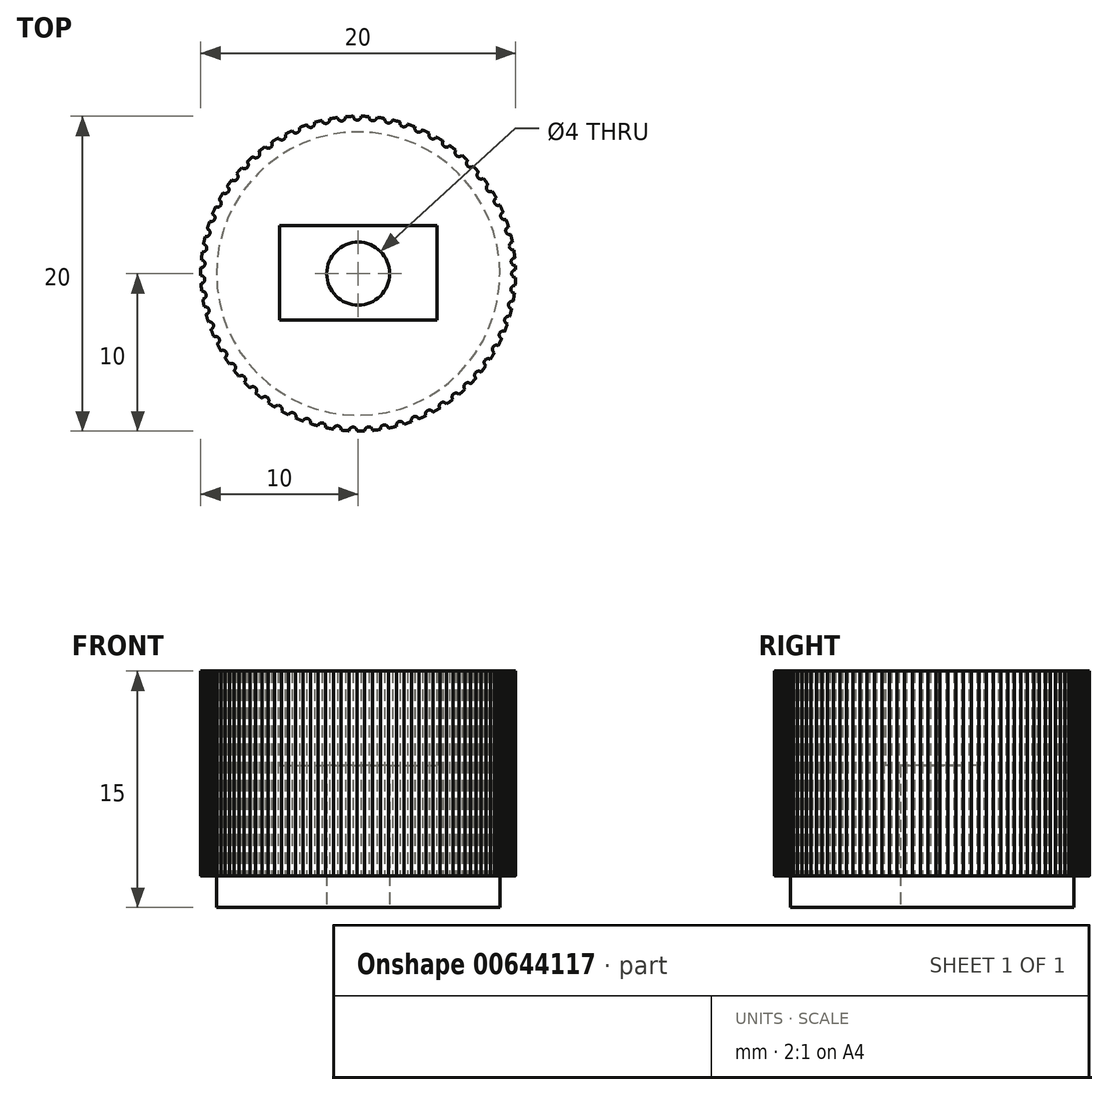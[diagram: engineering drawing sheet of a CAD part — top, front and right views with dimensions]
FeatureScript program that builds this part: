
annotation { "Feature Type Name" : "Feature", "Feature Type Description" : "" }
export const myFeature = defineFeature(function(context is Context, id is Id, definition is map)
    precondition{}
    {
        {
            var Q0;
            Q0=qCreatedBy(makeId("Top.planeOp"),FACE);
            var sketch = newSketch(context, id + "F0", { "sketchPlane" : qUnion([Q0])});
            skCircle(sketch, "E0", {"center": v(0, 0) * mm, "radius": 10 * mm});
            skLineSegment(sketch, "E1.bottom", {"start": v(-5, 3.04) * mm, "end": v(5, 3.04) * mm});
            skLineSegment(sketch, "E1.top", {"start": v(-5, -2.96) * mm, "end": v(5, -2.96) * mm});
            skLineSegment(sketch, "E1.left", {"start": v(-5, 3.04) * mm, "end": v(-5, -2.96) * mm});
            skLineSegment(sketch, "E1.right", {"start": v(5, 3.04) * mm, "end": v(5, -2.96) * mm});
            skCircle(sketch, "E2", {"center": v(0, 0) * mm, "radius": 2 * mm});
            skCircle(sketch, "E3", {"center": v(0, 0) * mm, "radius": 9 * mm});
            skCircle(sketch, "E4", {"center": v(10, 0) * mm, "radius": 0.25 * mm});
            skCircle(sketch, "E5", {"center": v(9.95, -1) * mm, "radius": 0.25 * mm});
            skCircle(sketch, "E6", {"center": v(9.8, -1.99) * mm, "radius": 0.25 * mm});
            skCircle(sketch, "E7", {"center": v(9.55, -2.96) * mm, "radius": 0.25 * mm});
            skCircle(sketch, "E8", {"center": v(9.2, -3.9) * mm, "radius": 0.25 * mm});
            skCircle(sketch, "E9", {"center": v(8.77, -4.8) * mm, "radius": 0.25 * mm});
            skCircle(sketch, "E10", {"center": v(8.25, -5.65) * mm, "radius": 0.25 * mm});
            skCircle(sketch, "E11", {"center": v(7.65, -6.45) * mm, "radius": 0.25 * mm});
            skCircle(sketch, "E12", {"center": v(6.96, -7.18) * mm, "radius": 0.25 * mm});
            skCircle(sketch, "E13", {"center": v(6.21, -7.84) * mm, "radius": 0.25 * mm});
            skCircle(sketch, "E14", {"center": v(5.4, -8.42) * mm, "radius": 0.25 * mm});
            skCircle(sketch, "E15", {"center": v(4.53, -8.91) * mm, "radius": 0.25 * mm});
            skCircle(sketch, "E16", {"center": v(3.62, -9.32) * mm, "radius": 0.25 * mm});
            skCircle(sketch, "E17", {"center": v(2.67, -9.64) * mm, "radius": 0.25 * mm});
            skCircle(sketch, "E18", {"center": v(1.67, -9.86) * mm, "radius": 0.25 * mm});
            skCircle(sketch, "E19", {"center": v(0.67, -9.98) * mm, "radius": 0.25 * mm});
            skCircle(sketch, "E20", {"center": v(-1.33, -9.91) * mm, "radius": 0.25 * mm});
            skCircle(sketch, "E21", {"center": v(-2.31, -9.73) * mm, "radius": 0.25 * mm});
            skCircle(sketch, "E22", {"center": v(-3.27, -9.45) * mm, "radius": 0.25 * mm});
            skCircle(sketch, "E23", {"center": v(-4.2, -9.08) * mm, "radius": 0.25 * mm});
            skCircle(sketch, "E24", {"center": v(-5.08, -8.61) * mm, "radius": 0.25 * mm});
            skCircle(sketch, "E25", {"center": v(-5.92, -8.06) * mm, "radius": 0.25 * mm});
            skCircle(sketch, "E26", {"center": v(-6.7, -7.43) * mm, "radius": 0.25 * mm});
            skCircle(sketch, "E27", {"center": v(-7.4, -6.72) * mm, "radius": 0.25 * mm});
            skCircle(sketch, "E28", {"center": v(-8.04, -5.95) * mm, "radius": 0.25 * mm});
            skCircle(sketch, "E29", {"center": v(-8.6, -5.12) * mm, "radius": 0.25 * mm});
            skCircle(sketch, "E30", {"center": v(-9.06, -4.23) * mm, "radius": 0.25 * mm});
            skCircle(sketch, "E31", {"center": v(-0.33, -10) * mm, "radius": 0.25 * mm});
            skCircle(sketch, "E32", {"center": v(-9.44, -3.3) * mm, "radius": 0.25 * mm});
            skCircle(sketch, "E33", {"center": v(-9.72, -2.35) * mm, "radius": 0.25 * mm});
            skCircle(sketch, "E34", {"center": v(-9.9, -1.37) * mm, "radius": 0.25 * mm});
            skCircle(sketch, "E35", {"center": v(-9.98, 0.63) * mm, "radius": 0.25 * mm});
            skCircle(sketch, "E36", {"center": v(-9.87, 1.62) * mm, "radius": 0.25 * mm});
            skCircle(sketch, "E37", {"center": v(-9.66, 2.6) * mm, "radius": 0.25 * mm});
            skCircle(sketch, "E38", {"center": v(-9.35, 3.55) * mm, "radius": 0.25 * mm});
            skCircle(sketch, "E39", {"center": v(-8.95, 4.47) * mm, "radius": 0.25 * mm});
            skCircle(sketch, "E40", {"center": v(-8.46, 5.34) * mm, "radius": 0.25 * mm});
            skCircle(sketch, "E41", {"center": v(-7.88, 6.16) * mm, "radius": 0.25 * mm});
            skCircle(sketch, "E42", {"center": v(-7.23, 6.91) * mm, "radius": 0.25 * mm});
            skCircle(sketch, "E43", {"center": v(-5.7, 8.21) * mm, "radius": 0.25 * mm});
            skCircle(sketch, "E44", {"center": v(-4.86, 8.74) * mm, "radius": 0.25 * mm});
            skCircle(sketch, "E45", {"center": v(-3.96, 9.18) * mm, "radius": 0.25 * mm});
            skCircle(sketch, "E46", {"center": v(-10, -0.37) * mm, "radius": 0.25 * mm});
            skCircle(sketch, "E47", {"center": v(-6.5, 7.6) * mm, "radius": 0.25 * mm});
            skCircle(sketch, "E48", {"center": v(-3.02, 9.53) * mm, "radius": 0.25 * mm});
            skCircle(sketch, "E49", {"center": v(-2.06, 9.79) * mm, "radius": 0.25 * mm});
            skCircle(sketch, "E50", {"center": v(-1.06, 9.94) * mm, "radius": 0.25 * mm});
            skCircle(sketch, "E51", {"center": v(-0.06, 10) * mm, "radius": 0.25 * mm});
            skCircle(sketch, "E52", {"center": v(0.94, 9.96) * mm, "radius": 0.25 * mm});
            skCircle(sketch, "E53", {"center": v(1.93, 9.81) * mm, "radius": 0.25 * mm});
            skCircle(sketch, "E54", {"center": v(2.9, 9.57) * mm, "radius": 0.25 * mm});
            skCircle(sketch, "E55", {"center": v(3.84, 9.23) * mm, "radius": 0.25 * mm});
            skCircle(sketch, "E56", {"center": v(4.75, 8.8) * mm, "radius": 0.25 * mm});
            skCircle(sketch, "E57", {"center": v(5.6, 8.28) * mm, "radius": 0.25 * mm});
            skCircle(sketch, "E58", {"center": v(6.4, 7.68) * mm, "radius": 0.25 * mm});
            skCircle(sketch, "E59", {"center": v(7.14, 7) * mm, "radius": 0.25 * mm});
            skCircle(sketch, "E60", {"center": v(7.8, 6.26) * mm, "radius": 0.25 * mm});
            skCircle(sketch, "E61", {"center": v(8.39, 5.45) * mm, "radius": 0.25 * mm});
            skCircle(sketch, "E62", {"center": v(8.89, 4.58) * mm, "radius": 0.25 * mm});
            skCircle(sketch, "E63", {"center": v(9.3, 3.67) * mm, "radius": 0.25 * mm});
            skCircle(sketch, "E64", {"center": v(9.62, 2.73) * mm, "radius": 0.25 * mm});
            skCircle(sketch, "E65", {"center": v(9.85, 1.75) * mm, "radius": 0.25 * mm});
            skCircle(sketch, "E66", {"center": v(9.97, 0.76) * mm, "radius": 0.25 * mm});
            skSolve(sketch);
        }
        {
            var Q0;
            Q0=makeQuery(id+"F0.imprint","IMPRINT",FACE,{"disambiguationData":[TD([[makeQuery(id+"F0.imprint","IMPRINT",EDGE,{"derivedFrom":sQuery(id+"F0.wireOp",EDGE,"E1.bottom")}),-1.0]])]});
            var Q1;
            Q1=makeQuery(id+"F0.imprint","IMPRINT",FACE,{"disambiguationData":[TD([[makeQuery(id+"F0.imprint","IMPRINT",EDGE,{"derivedFrom":sQuery(id+"F0.wireOp",EDGE,"E1.bottom")}),1.0]])]});
            extrude(context, id + "F1", {"entities" : qUnion([Q0, Q1]), "depth" : 15 * mm, "offsetDistance" : 25 * mm});
        }
        {
            var Q0;
            Q0=makeQuery(id+"F0.imprint","IMPRINT",FACE,{"disambiguationData":[TD([[makeQuery(id+"F0.imprint","IMPRINT",EDGE,{"derivedFrom":sQuery(id+"F0.wireOp",EDGE,"E0")}),1.0]])]});
            extrude(context, id + "F2", {"entities" : qUnion([Q0]), "operationType" : NewBodyOperationType.ADD, "depth" : 15 * mm, "offsetDistance" : 25 * mm, "hasSecondDirection" : true, "secondDirectionOppositeDirection" : false, "secondDirectionDepth" : 2 * mm});
        }
        {
            var Q0;
            Q0=makeQuery(id+"F0.imprint","IMPRINT",FACE,{"disambiguationData":[TD([[makeQuery(id+"F0.imprint","IMPRINT",EDGE,{"derivedFrom":sQuery(id+"F0.wireOp",EDGE,"E1.bottom")}),-1.0]])]});
            extrude(context, id + "F3", {"entities" : qUnion([Q0]), "operationType" : NewBodyOperationType.REMOVE, "depth" : 15 * mm, "offsetDistance" : 25 * mm, "hasSecondDirection" : true, "secondDirectionOppositeDirection" : false, "secondDirectionDepth" : 9 * mm});
        }
        {
            var Q0;
            {var subQ0=sQuery(id+"F0.wireOp",EDGE,"E4");var subQ1=sQuery(id+"F0.wireOp",EDGE,"E0");var subQ2=makeQuery(id+"F0.imprint","INTERSECT",VERTEX,{"disambiguationData":[OD(0.0)],"derivedFrom":[subQ1,subQ0]});Q0=makeQuery(id+"F0.imprint","IMPRINT",FACE,{"disambiguationData":[TD([[makeQuery(id+"F0.imprint","IMPRINT",EDGE,{"disambiguationData":[TD([[subQ2,1.0]])],"derivedFrom":subQ1}),1.0]])]});}
            var Q1;
            {var subQ0=sQuery(id+"F0.wireOp",EDGE,"E5");var subQ1=sQuery(id+"F0.wireOp",EDGE,"E0");var subQ2=makeQuery(id+"F0.imprint","INTERSECT",VERTEX,{"disambiguationData":[OD(0.0)],"derivedFrom":[subQ1,subQ0]});Q1=makeQuery(id+"F0.imprint","IMPRINT",FACE,{"disambiguationData":[TD([[makeQuery(id+"F0.imprint","IMPRINT",EDGE,{"disambiguationData":[TD([[subQ2,-1.0]])],"derivedFrom":subQ1}),1.0]])]});}
            var Q2;
            {var subQ0=sQuery(id+"F0.wireOp",EDGE,"E6");var subQ1=sQuery(id+"F0.wireOp",EDGE,"E0");var subQ2=makeQuery(id+"F0.imprint","INTERSECT",VERTEX,{"disambiguationData":[OD(0.0)],"derivedFrom":[subQ1,subQ0]});Q2=makeQuery(id+"F0.imprint","IMPRINT",FACE,{"disambiguationData":[TD([[makeQuery(id+"F0.imprint","IMPRINT",EDGE,{"disambiguationData":[TD([[subQ2,-1.0]])],"derivedFrom":subQ1}),1.0]])]});}
            extrude(context, id + "F4", {"entities" : qUnion([Q0, Q1, Q2]), "operationType" : NewBodyOperationType.REMOVE, "oppositeDirection" : true, "depth" : 25 * mm, "offsetDistance" : 25 * mm});
        }
        {
            var Q0;
            {var subQ0=sQuery(id+"F0.wireOp",EDGE,"E43");var subQ1=sQuery(id+"F0.wireOp",EDGE,"E0");var subQ2=makeQuery(id+"F0.imprint","INTERSECT",VERTEX,{"disambiguationData":[OD(0.0)],"derivedFrom":[subQ1,subQ0]});Q0=makeQuery(id+"F0.imprint","IMPRINT",FACE,{"disambiguationData":[TD([[makeQuery(id+"F0.imprint","IMPRINT",EDGE,{"disambiguationData":[TD([[subQ2,-1.0]])],"derivedFrom":subQ1}),1.0]])]});}
            var Q1;
            {var subQ0=sQuery(id+"F0.wireOp",EDGE,"E47");var subQ1=sQuery(id+"F0.wireOp",EDGE,"E0");var subQ2=makeQuery(id+"F0.imprint","INTERSECT",VERTEX,{"disambiguationData":[OD(0.0)],"derivedFrom":[subQ1,subQ0]});Q1=makeQuery(id+"F0.imprint","IMPRINT",FACE,{"disambiguationData":[TD([[makeQuery(id+"F0.imprint","IMPRINT",EDGE,{"disambiguationData":[TD([[subQ2,-1.0]])],"derivedFrom":subQ1}),1.0]])]});}
            var Q2;
            {var subQ0=sQuery(id+"F0.wireOp",EDGE,"E42");var subQ1=sQuery(id+"F0.wireOp",EDGE,"E0");var subQ2=makeQuery(id+"F0.imprint","INTERSECT",VERTEX,{"disambiguationData":[OD(0.0)],"derivedFrom":[subQ1,subQ0]});Q2=makeQuery(id+"F0.imprint","IMPRINT",FACE,{"disambiguationData":[TD([[makeQuery(id+"F0.imprint","IMPRINT",EDGE,{"disambiguationData":[TD([[subQ2,-1.0]])],"derivedFrom":subQ1}),1.0]])]});}
            var Q3;
            {var subQ0=sQuery(id+"F0.wireOp",EDGE,"E41");var subQ1=sQuery(id+"F0.wireOp",EDGE,"E0");var subQ2=makeQuery(id+"F0.imprint","INTERSECT",VERTEX,{"disambiguationData":[OD(0.0)],"derivedFrom":[subQ1,subQ0]});Q3=makeQuery(id+"F0.imprint","IMPRINT",FACE,{"disambiguationData":[TD([[makeQuery(id+"F0.imprint","IMPRINT",EDGE,{"disambiguationData":[TD([[subQ2,-1.0]])],"derivedFrom":subQ1}),1.0]])]});}
            var Q4;
            {var subQ0=sQuery(id+"F0.wireOp",EDGE,"E40");var subQ1=sQuery(id+"F0.wireOp",EDGE,"E0");var subQ2=makeQuery(id+"F0.imprint","INTERSECT",VERTEX,{"disambiguationData":[OD(0.0)],"derivedFrom":[subQ1,subQ0]});Q4=makeQuery(id+"F0.imprint","IMPRINT",FACE,{"disambiguationData":[TD([[makeQuery(id+"F0.imprint","IMPRINT",EDGE,{"disambiguationData":[TD([[subQ2,-1.0]])],"derivedFrom":subQ1}),1.0]])]});}
            var Q5;
            {var subQ0=sQuery(id+"F0.wireOp",EDGE,"E39");var subQ1=sQuery(id+"F0.wireOp",EDGE,"E0");var subQ2=makeQuery(id+"F0.imprint","INTERSECT",VERTEX,{"disambiguationData":[OD(0.0)],"derivedFrom":[subQ1,subQ0]});Q5=makeQuery(id+"F0.imprint","IMPRINT",FACE,{"disambiguationData":[TD([[makeQuery(id+"F0.imprint","IMPRINT",EDGE,{"disambiguationData":[TD([[subQ2,-1.0]])],"derivedFrom":subQ1}),1.0]])]});}
            var Q6;
            {var subQ0=sQuery(id+"F0.wireOp",EDGE,"E38");var subQ1=sQuery(id+"F0.wireOp",EDGE,"E0");var subQ2=makeQuery(id+"F0.imprint","INTERSECT",VERTEX,{"disambiguationData":[OD(0.0)],"derivedFrom":[subQ1,subQ0]});Q6=makeQuery(id+"F0.imprint","IMPRINT",FACE,{"disambiguationData":[TD([[makeQuery(id+"F0.imprint","IMPRINT",EDGE,{"disambiguationData":[TD([[subQ2,-1.0]])],"derivedFrom":subQ1}),1.0]])]});}
            var Q7;
            {var subQ0=sQuery(id+"F0.wireOp",EDGE,"E37");var subQ1=sQuery(id+"F0.wireOp",EDGE,"E0");var subQ2=makeQuery(id+"F0.imprint","INTERSECT",VERTEX,{"disambiguationData":[OD(0.0)],"derivedFrom":[subQ1,subQ0]});Q7=makeQuery(id+"F0.imprint","IMPRINT",FACE,{"disambiguationData":[TD([[makeQuery(id+"F0.imprint","IMPRINT",EDGE,{"disambiguationData":[TD([[subQ2,-1.0]])],"derivedFrom":subQ1}),1.0]])]});}
            var Q8;
            {var subQ0=sQuery(id+"F0.wireOp",EDGE,"E36");var subQ1=sQuery(id+"F0.wireOp",EDGE,"E0");var subQ2=makeQuery(id+"F0.imprint","INTERSECT",VERTEX,{"disambiguationData":[OD(0.0)],"derivedFrom":[subQ1,subQ0]});Q8=makeQuery(id+"F0.imprint","IMPRINT",FACE,{"disambiguationData":[TD([[makeQuery(id+"F0.imprint","IMPRINT",EDGE,{"disambiguationData":[TD([[subQ2,-1.0]])],"derivedFrom":subQ1}),1.0]])]});}
            var Q9;
            {var subQ0=sQuery(id+"F0.wireOp",EDGE,"E35");var subQ1=sQuery(id+"F0.wireOp",EDGE,"E0");var subQ2=makeQuery(id+"F0.imprint","INTERSECT",VERTEX,{"disambiguationData":[OD(0.0)],"derivedFrom":[subQ1,subQ0]});Q9=makeQuery(id+"F0.imprint","IMPRINT",FACE,{"disambiguationData":[TD([[makeQuery(id+"F0.imprint","IMPRINT",EDGE,{"disambiguationData":[TD([[subQ2,-1.0]])],"derivedFrom":subQ1}),1.0]])]});}
            var Q10;
            {var subQ0=sQuery(id+"F0.wireOp",EDGE,"E46");var subQ1=sQuery(id+"F0.wireOp",EDGE,"E0");var subQ2=makeQuery(id+"F0.imprint","INTERSECT",VERTEX,{"disambiguationData":[OD(0.0)],"derivedFrom":[subQ1,subQ0]});Q10=makeQuery(id+"F0.imprint","IMPRINT",FACE,{"disambiguationData":[TD([[makeQuery(id+"F0.imprint","IMPRINT",EDGE,{"disambiguationData":[TD([[subQ2,-1.0]])],"derivedFrom":subQ1}),1.0]])]});}
            var Q11;
            {var subQ0=sQuery(id+"F0.wireOp",EDGE,"E34");var subQ1=sQuery(id+"F0.wireOp",EDGE,"E0");var subQ2=makeQuery(id+"F0.imprint","INTERSECT",VERTEX,{"disambiguationData":[OD(0.0)],"derivedFrom":[subQ1,subQ0]});Q11=makeQuery(id+"F0.imprint","IMPRINT",FACE,{"disambiguationData":[TD([[makeQuery(id+"F0.imprint","IMPRINT",EDGE,{"disambiguationData":[TD([[subQ2,-1.0]])],"derivedFrom":subQ1}),1.0]])]});}
            var Q12;
            {var subQ0=sQuery(id+"F0.wireOp",EDGE,"E33");var subQ1=sQuery(id+"F0.wireOp",EDGE,"E0");var subQ2=makeQuery(id+"F0.imprint","INTERSECT",VERTEX,{"disambiguationData":[OD(0.0)],"derivedFrom":[subQ1,subQ0]});Q12=makeQuery(id+"F0.imprint","IMPRINT",FACE,{"disambiguationData":[TD([[makeQuery(id+"F0.imprint","IMPRINT",EDGE,{"disambiguationData":[TD([[subQ2,-1.0]])],"derivedFrom":subQ1}),1.0]])]});}
            var Q13;
            {var subQ0=sQuery(id+"F0.wireOp",EDGE,"E32");var subQ1=sQuery(id+"F0.wireOp",EDGE,"E0");var subQ2=makeQuery(id+"F0.imprint","INTERSECT",VERTEX,{"disambiguationData":[OD(0.0)],"derivedFrom":[subQ1,subQ0]});Q13=makeQuery(id+"F0.imprint","IMPRINT",FACE,{"disambiguationData":[TD([[makeQuery(id+"F0.imprint","IMPRINT",EDGE,{"disambiguationData":[TD([[subQ2,-1.0]])],"derivedFrom":subQ1}),1.0]])]});}
            var Q14;
            {var subQ0=sQuery(id+"F0.wireOp",EDGE,"E30");var subQ1=sQuery(id+"F0.wireOp",EDGE,"E0");var subQ2=makeQuery(id+"F0.imprint","INTERSECT",VERTEX,{"disambiguationData":[OD(0.0)],"derivedFrom":[subQ1,subQ0]});Q14=makeQuery(id+"F0.imprint","IMPRINT",FACE,{"disambiguationData":[TD([[makeQuery(id+"F0.imprint","IMPRINT",EDGE,{"disambiguationData":[TD([[subQ2,-1.0]])],"derivedFrom":subQ1}),1.0]])]});}
            var Q15;
            {var subQ0=sQuery(id+"F0.wireOp",EDGE,"E29");var subQ1=sQuery(id+"F0.wireOp",EDGE,"E0");var subQ2=makeQuery(id+"F0.imprint","INTERSECT",VERTEX,{"disambiguationData":[OD(0.0)],"derivedFrom":[subQ1,subQ0]});Q15=makeQuery(id+"F0.imprint","IMPRINT",FACE,{"disambiguationData":[TD([[makeQuery(id+"F0.imprint","IMPRINT",EDGE,{"disambiguationData":[TD([[subQ2,-1.0]])],"derivedFrom":subQ1}),1.0]])]});}
            var Q16;
            {var subQ0=sQuery(id+"F0.wireOp",EDGE,"E28");var subQ1=sQuery(id+"F0.wireOp",EDGE,"E0");var subQ2=makeQuery(id+"F0.imprint","INTERSECT",VERTEX,{"disambiguationData":[OD(0.0)],"derivedFrom":[subQ1,subQ0]});Q16=makeQuery(id+"F0.imprint","IMPRINT",FACE,{"disambiguationData":[TD([[makeQuery(id+"F0.imprint","IMPRINT",EDGE,{"disambiguationData":[TD([[subQ2,-1.0]])],"derivedFrom":subQ1}),1.0]])]});}
            var Q17;
            {var subQ0=sQuery(id+"F0.wireOp",EDGE,"E27");var subQ1=sQuery(id+"F0.wireOp",EDGE,"E0");var subQ2=makeQuery(id+"F0.imprint","INTERSECT",VERTEX,{"disambiguationData":[OD(0.0)],"derivedFrom":[subQ1,subQ0]});Q17=makeQuery(id+"F0.imprint","IMPRINT",FACE,{"disambiguationData":[TD([[makeQuery(id+"F0.imprint","IMPRINT",EDGE,{"disambiguationData":[TD([[subQ2,-1.0]])],"derivedFrom":subQ1}),1.0]])]});}
            var Q18;
            {var subQ0=sQuery(id+"F0.wireOp",EDGE,"E26");var subQ1=sQuery(id+"F0.wireOp",EDGE,"E0");var subQ2=makeQuery(id+"F0.imprint","INTERSECT",VERTEX,{"disambiguationData":[OD(0.0)],"derivedFrom":[subQ1,subQ0]});Q18=makeQuery(id+"F0.imprint","IMPRINT",FACE,{"disambiguationData":[TD([[makeQuery(id+"F0.imprint","IMPRINT",EDGE,{"disambiguationData":[TD([[subQ2,-1.0]])],"derivedFrom":subQ1}),1.0]])]});}
            var Q19;
            {var subQ0=sQuery(id+"F0.wireOp",EDGE,"E25");var subQ1=sQuery(id+"F0.wireOp",EDGE,"E0");var subQ2=makeQuery(id+"F0.imprint","INTERSECT",VERTEX,{"disambiguationData":[OD(0.0)],"derivedFrom":[subQ1,subQ0]});Q19=makeQuery(id+"F0.imprint","IMPRINT",FACE,{"disambiguationData":[TD([[makeQuery(id+"F0.imprint","IMPRINT",EDGE,{"disambiguationData":[TD([[subQ2,-1.0]])],"derivedFrom":subQ1}),1.0]])]});}
            var Q20;
            {var subQ0=sQuery(id+"F0.wireOp",EDGE,"E24");var subQ1=sQuery(id+"F0.wireOp",EDGE,"E0");var subQ2=makeQuery(id+"F0.imprint","INTERSECT",VERTEX,{"disambiguationData":[OD(0.0)],"derivedFrom":[subQ1,subQ0]});Q20=makeQuery(id+"F0.imprint","IMPRINT",FACE,{"disambiguationData":[TD([[makeQuery(id+"F0.imprint","IMPRINT",EDGE,{"disambiguationData":[TD([[subQ2,-1.0]])],"derivedFrom":subQ1}),1.0]])]});}
            var Q21;
            {var subQ0=sQuery(id+"F0.wireOp",EDGE,"E23");var subQ1=sQuery(id+"F0.wireOp",EDGE,"E0");var subQ2=makeQuery(id+"F0.imprint","INTERSECT",VERTEX,{"disambiguationData":[OD(0.0)],"derivedFrom":[subQ1,subQ0]});Q21=makeQuery(id+"F0.imprint","IMPRINT",FACE,{"disambiguationData":[TD([[makeQuery(id+"F0.imprint","IMPRINT",EDGE,{"disambiguationData":[TD([[subQ2,-1.0]])],"derivedFrom":subQ1}),1.0]])]});}
            var Q22;
            {var subQ0=sQuery(id+"F0.wireOp",EDGE,"E22");var subQ1=sQuery(id+"F0.wireOp",EDGE,"E0");var subQ2=makeQuery(id+"F0.imprint","INTERSECT",VERTEX,{"disambiguationData":[OD(0.0)],"derivedFrom":[subQ1,subQ0]});Q22=makeQuery(id+"F0.imprint","IMPRINT",FACE,{"disambiguationData":[TD([[makeQuery(id+"F0.imprint","IMPRINT",EDGE,{"disambiguationData":[TD([[subQ2,-1.0]])],"derivedFrom":subQ1}),1.0]])]});}
            var Q23;
            {var subQ0=sQuery(id+"F0.wireOp",EDGE,"E21");var subQ1=sQuery(id+"F0.wireOp",EDGE,"E0");var subQ2=makeQuery(id+"F0.imprint","INTERSECT",VERTEX,{"disambiguationData":[OD(0.0)],"derivedFrom":[subQ1,subQ0]});Q23=makeQuery(id+"F0.imprint","IMPRINT",FACE,{"disambiguationData":[TD([[makeQuery(id+"F0.imprint","IMPRINT",EDGE,{"disambiguationData":[TD([[subQ2,-1.0]])],"derivedFrom":subQ1}),1.0]])]});}
            var Q24;
            {var subQ0=sQuery(id+"F0.wireOp",EDGE,"E20");var subQ1=sQuery(id+"F0.wireOp",EDGE,"E0");var subQ2=makeQuery(id+"F0.imprint","INTERSECT",VERTEX,{"disambiguationData":[OD(0.0)],"derivedFrom":[subQ1,subQ0]});Q24=makeQuery(id+"F0.imprint","IMPRINT",FACE,{"disambiguationData":[TD([[makeQuery(id+"F0.imprint","IMPRINT",EDGE,{"disambiguationData":[TD([[subQ2,-1.0]])],"derivedFrom":subQ1}),1.0]])]});}
            var Q25;
            {var subQ0=sQuery(id+"F0.wireOp",EDGE,"E31");var subQ1=sQuery(id+"F0.wireOp",EDGE,"E0");var subQ2=makeQuery(id+"F0.imprint","INTERSECT",VERTEX,{"disambiguationData":[OD(0.0)],"derivedFrom":[subQ1,subQ0]});Q25=makeQuery(id+"F0.imprint","IMPRINT",FACE,{"disambiguationData":[TD([[makeQuery(id+"F0.imprint","IMPRINT",EDGE,{"disambiguationData":[TD([[subQ2,-1.0]])],"derivedFrom":subQ1}),1.0]])]});}
            var Q26;
            {var subQ0=sQuery(id+"F0.wireOp",EDGE,"E19");var subQ1=sQuery(id+"F0.wireOp",EDGE,"E0");var subQ2=makeQuery(id+"F0.imprint","INTERSECT",VERTEX,{"disambiguationData":[OD(0.0)],"derivedFrom":[subQ1,subQ0]});Q26=makeQuery(id+"F0.imprint","IMPRINT",FACE,{"disambiguationData":[TD([[makeQuery(id+"F0.imprint","IMPRINT",EDGE,{"disambiguationData":[TD([[subQ2,-1.0]])],"derivedFrom":subQ1}),1.0]])]});}
            var Q27;
            {var subQ0=sQuery(id+"F0.wireOp",EDGE,"E18");var subQ1=sQuery(id+"F0.wireOp",EDGE,"E0");var subQ2=makeQuery(id+"F0.imprint","INTERSECT",VERTEX,{"disambiguationData":[OD(0.0)],"derivedFrom":[subQ1,subQ0]});Q27=makeQuery(id+"F0.imprint","IMPRINT",FACE,{"disambiguationData":[TD([[makeQuery(id+"F0.imprint","IMPRINT",EDGE,{"disambiguationData":[TD([[subQ2,-1.0]])],"derivedFrom":subQ1}),1.0]])]});}
            var Q28;
            {var subQ0=sQuery(id+"F0.wireOp",EDGE,"E17");var subQ1=sQuery(id+"F0.wireOp",EDGE,"E0");var subQ2=makeQuery(id+"F0.imprint","INTERSECT",VERTEX,{"disambiguationData":[OD(0.0)],"derivedFrom":[subQ1,subQ0]});Q28=makeQuery(id+"F0.imprint","IMPRINT",FACE,{"disambiguationData":[TD([[makeQuery(id+"F0.imprint","IMPRINT",EDGE,{"disambiguationData":[TD([[subQ2,-1.0]])],"derivedFrom":subQ1}),1.0]])]});}
            var Q29;
            {var subQ0=sQuery(id+"F0.wireOp",EDGE,"E16");var subQ1=sQuery(id+"F0.wireOp",EDGE,"E0");var subQ2=makeQuery(id+"F0.imprint","INTERSECT",VERTEX,{"disambiguationData":[OD(0.0)],"derivedFrom":[subQ1,subQ0]});Q29=makeQuery(id+"F0.imprint","IMPRINT",FACE,{"disambiguationData":[TD([[makeQuery(id+"F0.imprint","IMPRINT",EDGE,{"disambiguationData":[TD([[subQ2,-1.0]])],"derivedFrom":subQ1}),1.0]])]});}
            var Q30;
            {var subQ0=sQuery(id+"F0.wireOp",EDGE,"E15");var subQ1=sQuery(id+"F0.wireOp",EDGE,"E0");var subQ2=makeQuery(id+"F0.imprint","INTERSECT",VERTEX,{"disambiguationData":[OD(0.0)],"derivedFrom":[subQ1,subQ0]});Q30=makeQuery(id+"F0.imprint","IMPRINT",FACE,{"disambiguationData":[TD([[makeQuery(id+"F0.imprint","IMPRINT",EDGE,{"disambiguationData":[TD([[subQ2,-1.0]])],"derivedFrom":subQ1}),1.0]])]});}
            var Q31;
            {var subQ0=sQuery(id+"F0.wireOp",EDGE,"E14");var subQ1=sQuery(id+"F0.wireOp",EDGE,"E0");var subQ2=makeQuery(id+"F0.imprint","INTERSECT",VERTEX,{"disambiguationData":[OD(0.0)],"derivedFrom":[subQ1,subQ0]});Q31=makeQuery(id+"F0.imprint","IMPRINT",FACE,{"disambiguationData":[TD([[makeQuery(id+"F0.imprint","IMPRINT",EDGE,{"disambiguationData":[TD([[subQ2,-1.0]])],"derivedFrom":subQ1}),1.0]])]});}
            var Q32;
            {var subQ0=sQuery(id+"F0.wireOp",EDGE,"E13");var subQ1=sQuery(id+"F0.wireOp",EDGE,"E0");var subQ2=makeQuery(id+"F0.imprint","INTERSECT",VERTEX,{"disambiguationData":[OD(0.0)],"derivedFrom":[subQ1,subQ0]});Q32=makeQuery(id+"F0.imprint","IMPRINT",FACE,{"disambiguationData":[TD([[makeQuery(id+"F0.imprint","IMPRINT",EDGE,{"disambiguationData":[TD([[subQ2,-1.0]])],"derivedFrom":subQ1}),1.0]])]});}
            var Q33;
            {var subQ0=sQuery(id+"F0.wireOp",EDGE,"E12");var subQ1=sQuery(id+"F0.wireOp",EDGE,"E0");var subQ2=makeQuery(id+"F0.imprint","INTERSECT",VERTEX,{"disambiguationData":[OD(0.0)],"derivedFrom":[subQ1,subQ0]});Q33=makeQuery(id+"F0.imprint","IMPRINT",FACE,{"disambiguationData":[TD([[makeQuery(id+"F0.imprint","IMPRINT",EDGE,{"disambiguationData":[TD([[subQ2,-1.0]])],"derivedFrom":subQ1}),1.0]])]});}
            var Q34;
            {var subQ0=sQuery(id+"F0.wireOp",EDGE,"E11");var subQ1=sQuery(id+"F0.wireOp",EDGE,"E0");var subQ2=makeQuery(id+"F0.imprint","INTERSECT",VERTEX,{"disambiguationData":[OD(0.0)],"derivedFrom":[subQ1,subQ0]});Q34=makeQuery(id+"F0.imprint","IMPRINT",FACE,{"disambiguationData":[TD([[makeQuery(id+"F0.imprint","IMPRINT",EDGE,{"disambiguationData":[TD([[subQ2,-1.0]])],"derivedFrom":subQ1}),1.0]])]});}
            var Q35;
            {var subQ0=sQuery(id+"F0.wireOp",EDGE,"E10");var subQ1=sQuery(id+"F0.wireOp",EDGE,"E0");var subQ2=makeQuery(id+"F0.imprint","INTERSECT",VERTEX,{"disambiguationData":[OD(0.0)],"derivedFrom":[subQ1,subQ0]});Q35=makeQuery(id+"F0.imprint","IMPRINT",FACE,{"disambiguationData":[TD([[makeQuery(id+"F0.imprint","IMPRINT",EDGE,{"disambiguationData":[TD([[subQ2,-1.0]])],"derivedFrom":subQ1}),1.0]])]});}
            var Q36;
            {var subQ0=sQuery(id+"F0.wireOp",EDGE,"E9");var subQ1=sQuery(id+"F0.wireOp",EDGE,"E0");var subQ2=makeQuery(id+"F0.imprint","INTERSECT",VERTEX,{"disambiguationData":[OD(0.0)],"derivedFrom":[subQ1,subQ0]});Q36=makeQuery(id+"F0.imprint","IMPRINT",FACE,{"disambiguationData":[TD([[makeQuery(id+"F0.imprint","IMPRINT",EDGE,{"disambiguationData":[TD([[subQ2,-1.0]])],"derivedFrom":subQ1}),1.0]])]});}
            var Q37;
            {var subQ0=sQuery(id+"F0.wireOp",EDGE,"E8");var subQ1=sQuery(id+"F0.wireOp",EDGE,"E0");var subQ2=makeQuery(id+"F0.imprint","INTERSECT",VERTEX,{"disambiguationData":[OD(0.0)],"derivedFrom":[subQ1,subQ0]});Q37=makeQuery(id+"F0.imprint","IMPRINT",FACE,{"disambiguationData":[TD([[makeQuery(id+"F0.imprint","IMPRINT",EDGE,{"disambiguationData":[TD([[subQ2,-1.0]])],"derivedFrom":subQ1}),1.0]])]});}
            var Q38;
            {var subQ0=sQuery(id+"F0.wireOp",EDGE,"E7");var subQ1=sQuery(id+"F0.wireOp",EDGE,"E0");var subQ2=makeQuery(id+"F0.imprint","INTERSECT",VERTEX,{"disambiguationData":[OD(0.0)],"derivedFrom":[subQ1,subQ0]});Q38=makeQuery(id+"F0.imprint","IMPRINT",FACE,{"disambiguationData":[TD([[makeQuery(id+"F0.imprint","IMPRINT",EDGE,{"disambiguationData":[TD([[subQ2,-1.0]])],"derivedFrom":subQ1}),1.0]])]});}
            var Q39;
            {var subQ0=sQuery(id+"F0.wireOp",EDGE,"E6");var subQ1=sQuery(id+"F0.wireOp",EDGE,"E0");var subQ2=makeQuery(id+"F0.imprint","INTERSECT",VERTEX,{"disambiguationData":[OD(0.0)],"derivedFrom":[subQ1,subQ0]});Q39=makeQuery(id+"F0.imprint","IMPRINT",FACE,{"disambiguationData":[TD([[makeQuery(id+"F0.imprint","IMPRINT",EDGE,{"disambiguationData":[TD([[subQ2,-1.0]])],"derivedFrom":subQ1}),1.0]])]});}
            var Q40;
            {var subQ0=sQuery(id+"F0.wireOp",EDGE,"E5");var subQ1=sQuery(id+"F0.wireOp",EDGE,"E0");var subQ2=makeQuery(id+"F0.imprint","INTERSECT",VERTEX,{"disambiguationData":[OD(0.0)],"derivedFrom":[subQ1,subQ0]});Q40=makeQuery(id+"F0.imprint","IMPRINT",FACE,{"disambiguationData":[TD([[makeQuery(id+"F0.imprint","IMPRINT",EDGE,{"disambiguationData":[TD([[subQ2,-1.0]])],"derivedFrom":subQ1}),1.0]])]});}
            var Q41;
            {var subQ0=sQuery(id+"F0.wireOp",EDGE,"E4");var subQ1=sQuery(id+"F0.wireOp",EDGE,"E0");var subQ2=makeQuery(id+"F0.imprint","INTERSECT",VERTEX,{"disambiguationData":[OD(0.0)],"derivedFrom":[subQ1,subQ0]});Q41=makeQuery(id+"F0.imprint","IMPRINT",FACE,{"disambiguationData":[TD([[makeQuery(id+"F0.imprint","IMPRINT",EDGE,{"disambiguationData":[TD([[subQ2,1.0]])],"derivedFrom":subQ1}),1.0]])]});}
            var Q42;
            {var subQ0=sQuery(id+"F0.wireOp",EDGE,"E66");var subQ1=sQuery(id+"F0.wireOp",EDGE,"E0");var subQ2=makeQuery(id+"F0.imprint","INTERSECT",VERTEX,{"disambiguationData":[OD(0.0)],"derivedFrom":[subQ1,subQ0]});Q42=makeQuery(id+"F0.imprint","IMPRINT",FACE,{"disambiguationData":[TD([[makeQuery(id+"F0.imprint","IMPRINT",EDGE,{"disambiguationData":[TD([[subQ2,-1.0]])],"derivedFrom":subQ1}),1.0]])]});}
            var Q43;
            {var subQ0=sQuery(id+"F0.wireOp",EDGE,"E65");var subQ1=sQuery(id+"F0.wireOp",EDGE,"E0");var subQ2=makeQuery(id+"F0.imprint","INTERSECT",VERTEX,{"disambiguationData":[OD(0.0)],"derivedFrom":[subQ1,subQ0]});Q43=makeQuery(id+"F0.imprint","IMPRINT",FACE,{"disambiguationData":[TD([[makeQuery(id+"F0.imprint","IMPRINT",EDGE,{"disambiguationData":[TD([[subQ2,-1.0]])],"derivedFrom":subQ1}),1.0]])]});}
            var Q44;
            {var subQ0=sQuery(id+"F0.wireOp",EDGE,"E64");var subQ1=sQuery(id+"F0.wireOp",EDGE,"E0");var subQ2=makeQuery(id+"F0.imprint","INTERSECT",VERTEX,{"disambiguationData":[OD(0.0)],"derivedFrom":[subQ1,subQ0]});Q44=makeQuery(id+"F0.imprint","IMPRINT",FACE,{"disambiguationData":[TD([[makeQuery(id+"F0.imprint","IMPRINT",EDGE,{"disambiguationData":[TD([[subQ2,-1.0]])],"derivedFrom":subQ1}),1.0]])]});}
            var Q45;
            {var subQ0=sQuery(id+"F0.wireOp",EDGE,"E63");var subQ1=sQuery(id+"F0.wireOp",EDGE,"E0");var subQ2=makeQuery(id+"F0.imprint","INTERSECT",VERTEX,{"disambiguationData":[OD(0.0)],"derivedFrom":[subQ1,subQ0]});Q45=makeQuery(id+"F0.imprint","IMPRINT",FACE,{"disambiguationData":[TD([[makeQuery(id+"F0.imprint","IMPRINT",EDGE,{"disambiguationData":[TD([[subQ2,-1.0]])],"derivedFrom":subQ1}),1.0]])]});}
            var Q46;
            {var subQ0=sQuery(id+"F0.wireOp",EDGE,"E62");var subQ1=sQuery(id+"F0.wireOp",EDGE,"E0");var subQ2=makeQuery(id+"F0.imprint","INTERSECT",VERTEX,{"disambiguationData":[OD(0.0)],"derivedFrom":[subQ1,subQ0]});Q46=makeQuery(id+"F0.imprint","IMPRINT",FACE,{"disambiguationData":[TD([[makeQuery(id+"F0.imprint","IMPRINT",EDGE,{"disambiguationData":[TD([[subQ2,-1.0]])],"derivedFrom":subQ1}),1.0]])]});}
            var Q47;
            {var subQ0=sQuery(id+"F0.wireOp",EDGE,"E61");var subQ1=sQuery(id+"F0.wireOp",EDGE,"E0");var subQ2=makeQuery(id+"F0.imprint","INTERSECT",VERTEX,{"disambiguationData":[OD(0.0)],"derivedFrom":[subQ1,subQ0]});Q47=makeQuery(id+"F0.imprint","IMPRINT",FACE,{"disambiguationData":[TD([[makeQuery(id+"F0.imprint","IMPRINT",EDGE,{"disambiguationData":[TD([[subQ2,-1.0]])],"derivedFrom":subQ1}),1.0]])]});}
            var Q48;
            {var subQ0=sQuery(id+"F0.wireOp",EDGE,"E60");var subQ1=sQuery(id+"F0.wireOp",EDGE,"E0");var subQ2=makeQuery(id+"F0.imprint","INTERSECT",VERTEX,{"disambiguationData":[OD(0.0)],"derivedFrom":[subQ1,subQ0]});Q48=makeQuery(id+"F0.imprint","IMPRINT",FACE,{"disambiguationData":[TD([[makeQuery(id+"F0.imprint","IMPRINT",EDGE,{"disambiguationData":[TD([[subQ2,-1.0]])],"derivedFrom":subQ1}),1.0]])]});}
            var Q49;
            {var subQ0=sQuery(id+"F0.wireOp",EDGE,"E59");var subQ1=sQuery(id+"F0.wireOp",EDGE,"E0");var subQ2=makeQuery(id+"F0.imprint","INTERSECT",VERTEX,{"disambiguationData":[OD(0.0)],"derivedFrom":[subQ1,subQ0]});Q49=makeQuery(id+"F0.imprint","IMPRINT",FACE,{"disambiguationData":[TD([[makeQuery(id+"F0.imprint","IMPRINT",EDGE,{"disambiguationData":[TD([[subQ2,-1.0]])],"derivedFrom":subQ1}),1.0]])]});}
            var Q50;
            {var subQ0=sQuery(id+"F0.wireOp",EDGE,"E58");var subQ1=sQuery(id+"F0.wireOp",EDGE,"E0");var subQ2=makeQuery(id+"F0.imprint","INTERSECT",VERTEX,{"disambiguationData":[OD(0.0)],"derivedFrom":[subQ1,subQ0]});Q50=makeQuery(id+"F0.imprint","IMPRINT",FACE,{"disambiguationData":[TD([[makeQuery(id+"F0.imprint","IMPRINT",EDGE,{"disambiguationData":[TD([[subQ2,-1.0]])],"derivedFrom":subQ1}),1.0]])]});}
            var Q51;
            {var subQ0=sQuery(id+"F0.wireOp",EDGE,"E57");var subQ1=sQuery(id+"F0.wireOp",EDGE,"E0");var subQ2=makeQuery(id+"F0.imprint","INTERSECT",VERTEX,{"disambiguationData":[OD(0.0)],"derivedFrom":[subQ1,subQ0]});Q51=makeQuery(id+"F0.imprint","IMPRINT",FACE,{"disambiguationData":[TD([[makeQuery(id+"F0.imprint","IMPRINT",EDGE,{"disambiguationData":[TD([[subQ2,-1.0]])],"derivedFrom":subQ1}),1.0]])]});}
            var Q52;
            {var subQ0=sQuery(id+"F0.wireOp",EDGE,"E56");var subQ1=sQuery(id+"F0.wireOp",EDGE,"E0");var subQ2=makeQuery(id+"F0.imprint","INTERSECT",VERTEX,{"disambiguationData":[OD(0.0)],"derivedFrom":[subQ1,subQ0]});Q52=makeQuery(id+"F0.imprint","IMPRINT",FACE,{"disambiguationData":[TD([[makeQuery(id+"F0.imprint","IMPRINT",EDGE,{"disambiguationData":[TD([[subQ2,-1.0]])],"derivedFrom":subQ1}),1.0]])]});}
            var Q53;
            {var subQ0=sQuery(id+"F0.wireOp",EDGE,"E55");var subQ1=sQuery(id+"F0.wireOp",EDGE,"E0");var subQ2=makeQuery(id+"F0.imprint","INTERSECT",VERTEX,{"disambiguationData":[OD(0.0)],"derivedFrom":[subQ1,subQ0]});Q53=makeQuery(id+"F0.imprint","IMPRINT",FACE,{"disambiguationData":[TD([[makeQuery(id+"F0.imprint","IMPRINT",EDGE,{"disambiguationData":[TD([[subQ2,-1.0]])],"derivedFrom":subQ1}),1.0]])]});}
            var Q54;
            {var subQ0=sQuery(id+"F0.wireOp",EDGE,"E54");var subQ1=sQuery(id+"F0.wireOp",EDGE,"E0");var subQ2=makeQuery(id+"F0.imprint","INTERSECT",VERTEX,{"disambiguationData":[OD(0.0)],"derivedFrom":[subQ1,subQ0]});Q54=makeQuery(id+"F0.imprint","IMPRINT",FACE,{"disambiguationData":[TD([[makeQuery(id+"F0.imprint","IMPRINT",EDGE,{"disambiguationData":[TD([[subQ2,-1.0]])],"derivedFrom":subQ1}),1.0]])]});}
            var Q55;
            {var subQ0=sQuery(id+"F0.wireOp",EDGE,"E53");var subQ1=sQuery(id+"F0.wireOp",EDGE,"E0");var subQ2=makeQuery(id+"F0.imprint","INTERSECT",VERTEX,{"disambiguationData":[OD(0.0)],"derivedFrom":[subQ1,subQ0]});Q55=makeQuery(id+"F0.imprint","IMPRINT",FACE,{"disambiguationData":[TD([[makeQuery(id+"F0.imprint","IMPRINT",EDGE,{"disambiguationData":[TD([[subQ2,-1.0]])],"derivedFrom":subQ1}),1.0]])]});}
            var Q56;
            {var subQ0=sQuery(id+"F0.wireOp",EDGE,"E52");var subQ1=sQuery(id+"F0.wireOp",EDGE,"E0");var subQ2=makeQuery(id+"F0.imprint","INTERSECT",VERTEX,{"disambiguationData":[OD(0.0)],"derivedFrom":[subQ1,subQ0]});Q56=makeQuery(id+"F0.imprint","IMPRINT",FACE,{"disambiguationData":[TD([[makeQuery(id+"F0.imprint","IMPRINT",EDGE,{"disambiguationData":[TD([[subQ2,-1.0]])],"derivedFrom":subQ1}),1.0]])]});}
            var Q57;
            {var subQ0=sQuery(id+"F0.wireOp",EDGE,"E51");var subQ1=sQuery(id+"F0.wireOp",EDGE,"E0");var subQ2=makeQuery(id+"F0.imprint","INTERSECT",VERTEX,{"disambiguationData":[OD(0.0)],"derivedFrom":[subQ1,subQ0]});Q57=makeQuery(id+"F0.imprint","IMPRINT",FACE,{"disambiguationData":[TD([[makeQuery(id+"F0.imprint","IMPRINT",EDGE,{"disambiguationData":[TD([[subQ2,-1.0]])],"derivedFrom":subQ1}),1.0]])]});}
            var Q58;
            {var subQ0=sQuery(id+"F0.wireOp",EDGE,"E50");var subQ1=sQuery(id+"F0.wireOp",EDGE,"E0");var subQ2=makeQuery(id+"F0.imprint","INTERSECT",VERTEX,{"disambiguationData":[OD(0.0)],"derivedFrom":[subQ1,subQ0]});Q58=makeQuery(id+"F0.imprint","IMPRINT",FACE,{"disambiguationData":[TD([[makeQuery(id+"F0.imprint","IMPRINT",EDGE,{"disambiguationData":[TD([[subQ2,-1.0]])],"derivedFrom":subQ1}),1.0]])]});}
            var Q59;
            {var subQ0=sQuery(id+"F0.wireOp",EDGE,"E49");var subQ1=sQuery(id+"F0.wireOp",EDGE,"E0");var subQ2=makeQuery(id+"F0.imprint","INTERSECT",VERTEX,{"disambiguationData":[OD(0.0)],"derivedFrom":[subQ1,subQ0]});Q59=makeQuery(id+"F0.imprint","IMPRINT",FACE,{"disambiguationData":[TD([[makeQuery(id+"F0.imprint","IMPRINT",EDGE,{"disambiguationData":[TD([[subQ2,-1.0]])],"derivedFrom":subQ1}),1.0]])]});}
            var Q60;
            {var subQ0=sQuery(id+"F0.wireOp",EDGE,"E48");var subQ1=sQuery(id+"F0.wireOp",EDGE,"E0");var subQ2=makeQuery(id+"F0.imprint","INTERSECT",VERTEX,{"disambiguationData":[OD(0.0)],"derivedFrom":[subQ1,subQ0]});Q60=makeQuery(id+"F0.imprint","IMPRINT",FACE,{"disambiguationData":[TD([[makeQuery(id+"F0.imprint","IMPRINT",EDGE,{"disambiguationData":[TD([[subQ2,-1.0]])],"derivedFrom":subQ1}),1.0]])]});}
            var Q61;
            {var subQ0=sQuery(id+"F0.wireOp",EDGE,"E45");var subQ1=sQuery(id+"F0.wireOp",EDGE,"E0");var subQ2=makeQuery(id+"F0.imprint","INTERSECT",VERTEX,{"disambiguationData":[OD(0.0)],"derivedFrom":[subQ1,subQ0]});Q61=makeQuery(id+"F0.imprint","IMPRINT",FACE,{"disambiguationData":[TD([[makeQuery(id+"F0.imprint","IMPRINT",EDGE,{"disambiguationData":[TD([[subQ2,-1.0]])],"derivedFrom":subQ1}),1.0]])]});}
            var Q62;
            {var subQ0=sQuery(id+"F0.wireOp",EDGE,"E44");var subQ1=sQuery(id+"F0.wireOp",EDGE,"E0");var subQ2=makeQuery(id+"F0.imprint","INTERSECT",VERTEX,{"disambiguationData":[OD(0.0)],"derivedFrom":[subQ1,subQ0]});Q62=makeQuery(id+"F0.imprint","IMPRINT",FACE,{"disambiguationData":[TD([[makeQuery(id+"F0.imprint","IMPRINT",EDGE,{"disambiguationData":[TD([[subQ2,-1.0]])],"derivedFrom":subQ1}),1.0]])]});}
            extrude(context, id + "F5", {"entities" : qUnion([Q0, Q1, Q2, Q3, Q4, Q5, Q6, Q7, Q8, Q9, Q10, Q11, Q12, Q13, Q14, Q15, Q16, Q17, Q18, Q19, Q20, Q21, Q22, Q23, Q24, Q25, Q26, Q27, Q28, Q29, Q30, Q31, Q32, Q33, Q34, Q35, Q36, Q37, Q38, Q39, Q40, Q41, Q42, Q43, Q44, Q45, Q46, Q47, Q48, Q49, Q50, Q51, Q52, Q53, Q54, Q55, Q56, Q57, Q58, Q59, Q60, Q61, Q62]), "operationType" : NewBodyOperationType.REMOVE, "depth" : 25 * mm, "offsetDistance" : 25 * mm});
        }
    });
